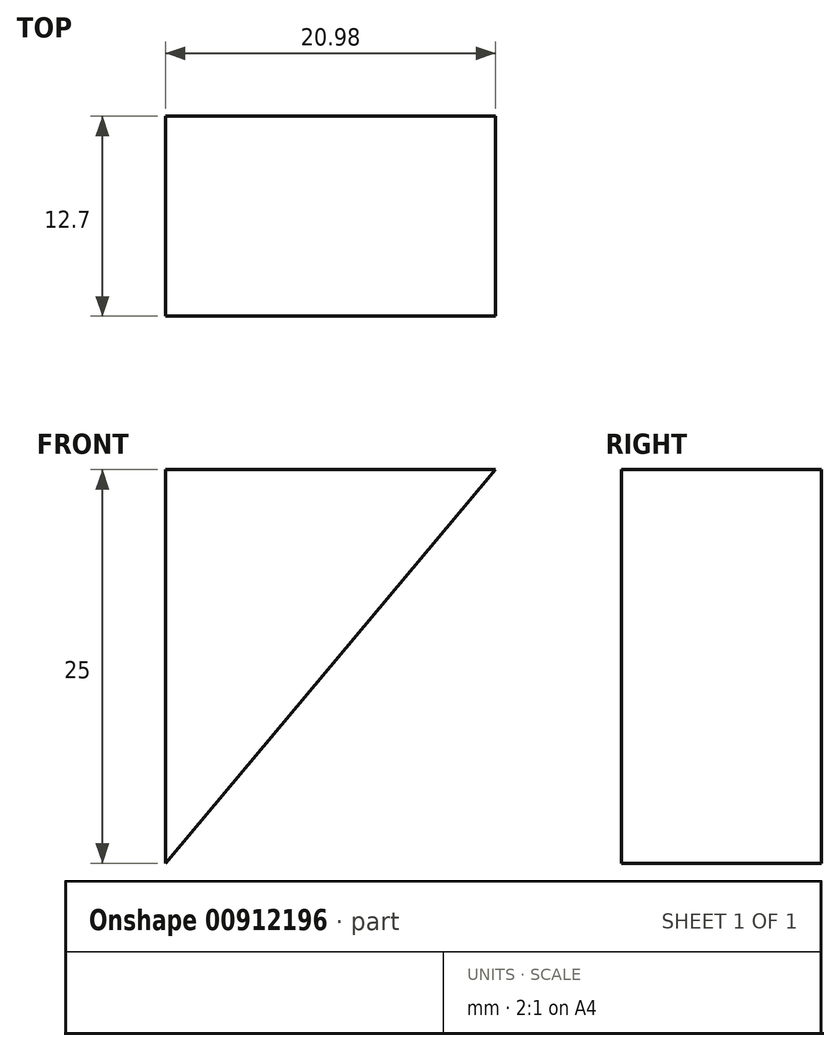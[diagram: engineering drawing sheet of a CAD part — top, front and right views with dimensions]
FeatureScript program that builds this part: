
annotation { "Feature Type Name" : "Feature", "Feature Type Description" : "" }
export const myFeature = defineFeature(function(context is Context, id is Id, definition is map)
    precondition{}
    {
        {
            var Q0;
            Q0=qCreatedBy(makeId("Front.planeOp"),FACE);
            var sketch = newSketch(context, id + "F0", { "sketchPlane" : qUnion([Q0])});
            skLineSegment(sketch, "E0", {"start": v(0, 0) * mm, "end": v(0, 25) * mm});
            skLineSegment(sketch, "E1", {"start": v(0, 25) * mm, "end": v(20.98, 25) * mm});
            skLineSegment(sketch, "E2", {"start": v(20.98, 25) * mm, "end": v(0, 0) * mm});
            skSolve(sketch);
        }
        {
            var Q0;
            Q0 = qSketchRegion(id + "F0", true);
            extrude(context, id + "F1", {"entities" : qUnion([Q0]), "depth" : 12.7 * mm, "offsetDistance" : 25 * mm});
        }
    });
